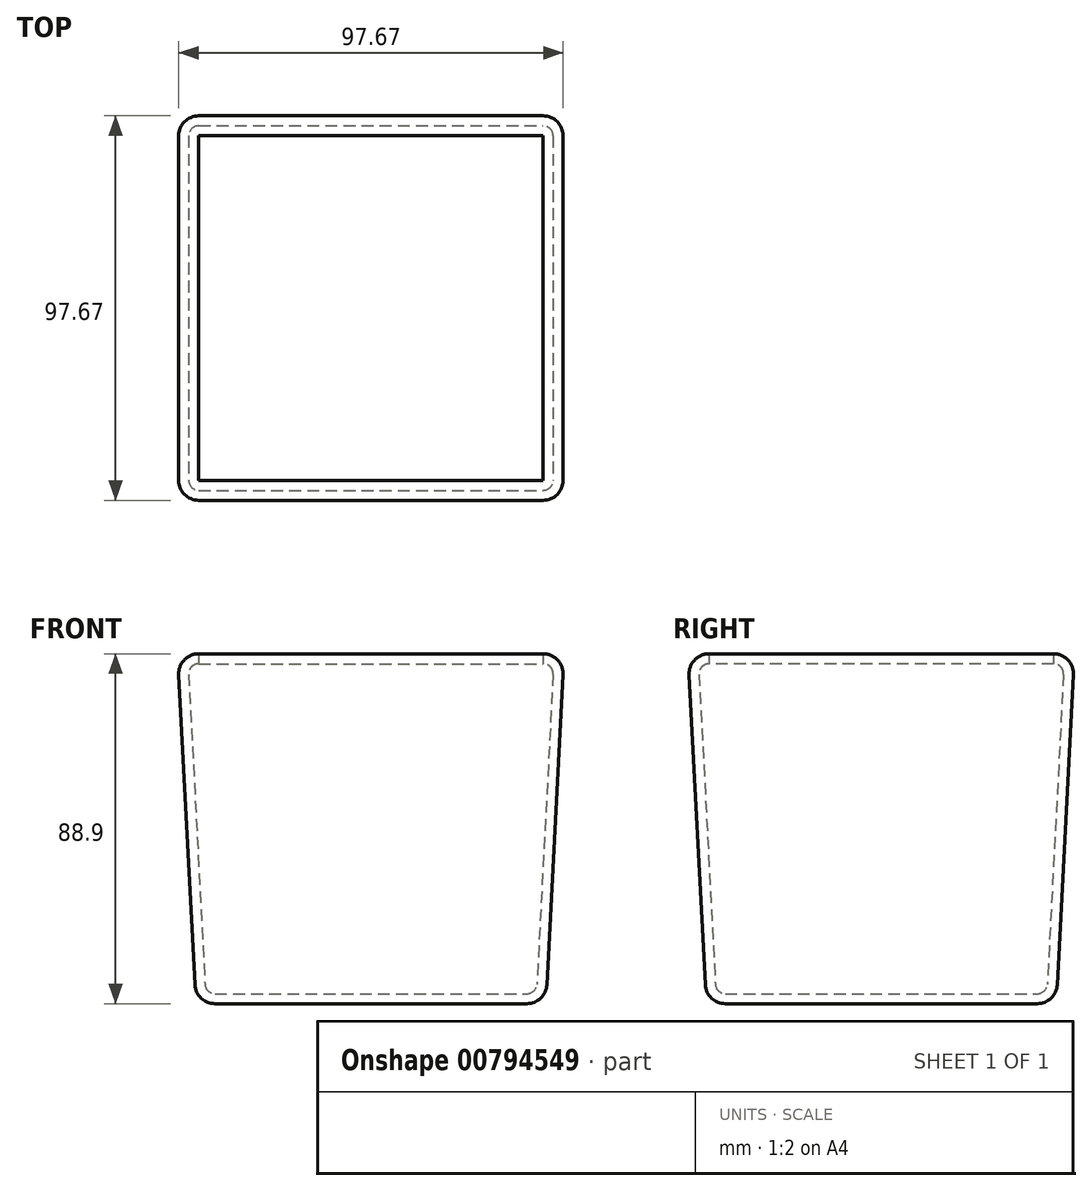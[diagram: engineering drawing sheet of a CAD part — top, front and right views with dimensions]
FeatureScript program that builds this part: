
annotation { "Feature Type Name" : "Feature", "Feature Type Description" : "" }
export const myFeature = defineFeature(function(context is Context, id is Id, definition is map)
    precondition{}
    {
        {
            var Q0;
            Q0=qCreatedBy(makeId("Top.planeOp"),FACE);
            var sketch = newSketch(context, id + "F0", { "sketchPlane" : qUnion([Q0])});
            skLineSegment(sketch, "E0.bottom", {"start": v(-47.6, 45.92) * mm, "end": v(41.3, 45.92) * mm});
            skLineSegment(sketch, "E0.top", {"start": v(-47.6, -42.98) * mm, "end": v(41.3, -42.98) * mm});
            skLineSegment(sketch, "E0.left", {"start": v(-47.6, 45.92) * mm, "end": v(-47.6, -42.98) * mm});
            skLineSegment(sketch, "E0.right", {"start": v(41.3, 45.92) * mm, "end": v(41.3, -42.98) * mm});
            skSolve(sketch);
        }
        {
            var Q0;
            Q0 = qSketchRegion(id + "F0", true);
            extrude(context, id + "F1", {"entities" : qUnion([Q0]), "depth" : 88.9 * mm, "offsetDistance" : 25.4 * mm, "hasDraft" : true, "draftAngle" : 3 * degree});
        }
        {
            var Q0;
            Q0=makeQuery(id+"F1.opExtrude","SWEPT_FACE",FACE,{"disambiguationData":[OSD([sQuery(id+"F0.wireOp",EDGE,"E0.top")])]});
            var Q1;
            Q1=makeQuery(id+"F1.opExtrude","SWEPT_FACE",FACE,{"disambiguationData":[OSD([sQuery(id+"F0.wireOp",EDGE,"E0.left")])]});
            var Q2;
            Q2=makeQuery(id+"F1.opExtrude","SWEPT_FACE",FACE,{"disambiguationData":[OSD([sQuery(id+"F0.wireOp",EDGE,"E0.right")])]});
            var Q3;
            Q3=makeQuery(id+"F1.opExtrude","SWEPT_FACE",FACE,{"disambiguationData":[OSD([sQuery(id+"F0.wireOp",EDGE,"E0.bottom")])]});
            fillet(context, id + "F2", {"entities" : qUnion([Q0, Q1, Q2, Q3]), "radius" : 5.08 * mm, "tangentPropagation" : true, "allowEdgeOverflow" : false});
        }
        {
            var Q0;
            Q0=makeQuery(id+"F1.opExtrude","CAP_FACE",FACE,{"disambiguationData":[OSD([sQuery(id+"F0.wireOp",EDGE,"E0.bottom"),sQuery(id+"F0.wireOp",EDGE,"E0.top"),sQuery(id+"F0.wireOp",EDGE,"E0.left"),sQuery(id+"F0.wireOp",EDGE,"E0.right")])],"isStart":false});
            shell(context, id + "F3", {"entities" : qUnion([Q0]), "thickness" : 2.54 * mm});
        }
    });
